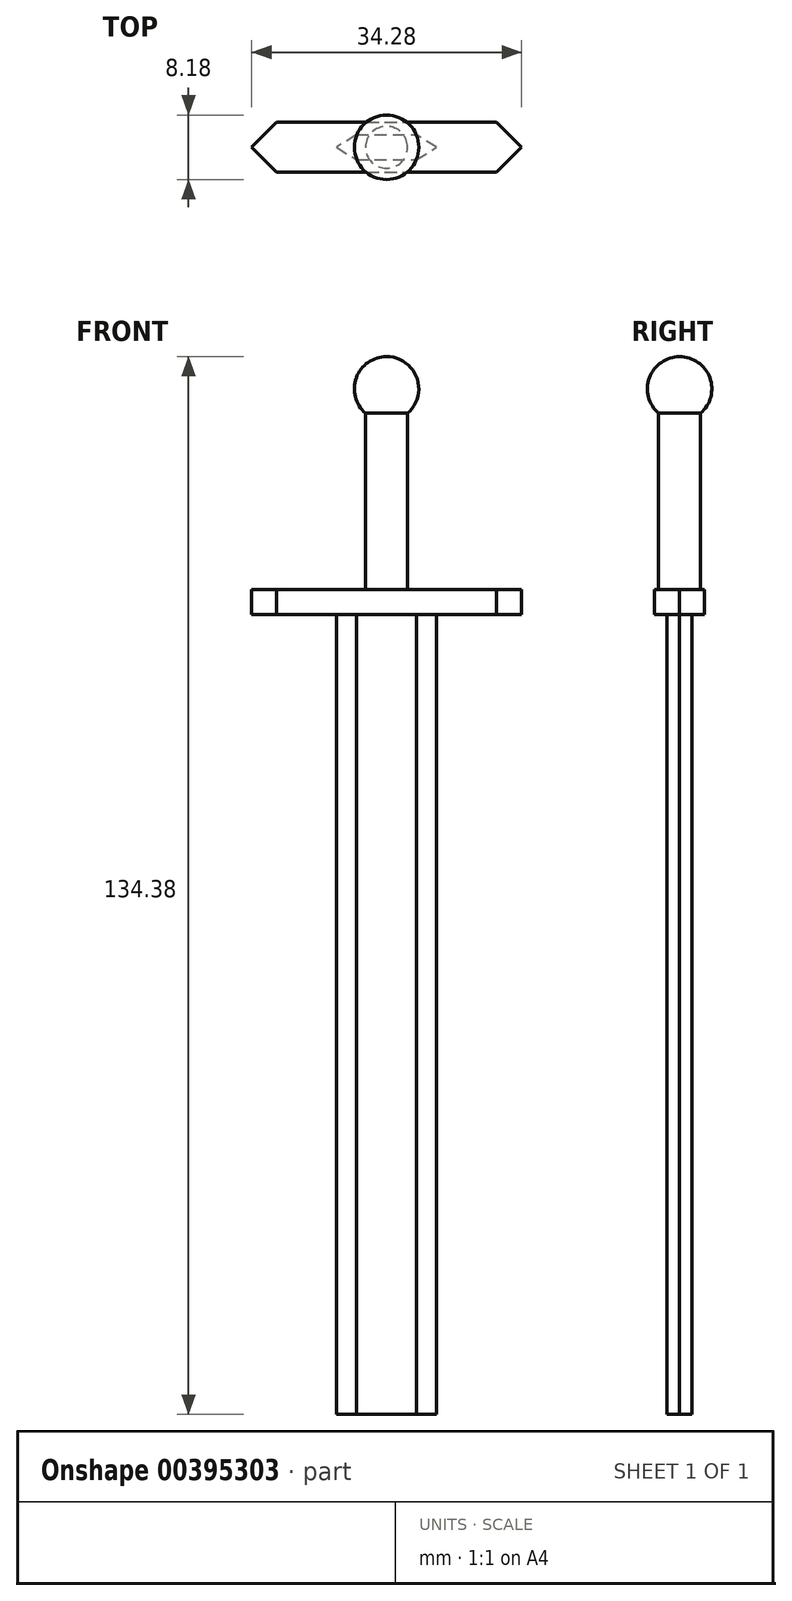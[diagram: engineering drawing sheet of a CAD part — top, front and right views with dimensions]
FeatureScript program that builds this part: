
annotation { "Feature Type Name" : "Feature", "Feature Type Description" : "" }
export const myFeature = defineFeature(function(context is Context, id is Id, definition is map)
    precondition{}
    {
        {
            var Q0;
            Q0=qCreatedBy(makeId("Top.planeOp"),FACE);
            var sketch = newSketch(context, id + "F0", { "sketchPlane" : qUnion([Q0])});
            skLineSegment(sketch, "E0.bottom", {"start": v(-3.81, 1.59) * mm, "end": v(0, 1.59) * mm});
            skLineSegment(sketch, "E0.top", {"start": v(-3.81, -1.59) * mm, "end": v(0, -1.59) * mm});
            skLineSegment(sketch, "E1", {"start": v(-3.81, 1.59) * mm, "end": v(-6.35, 0) * mm});
            skLineSegment(sketch, "E2", {"start": v(-6.35, 0) * mm, "end": v(-3.81, -1.59) * mm});
            skPoint(sketch, "E3.start.orphan", {"position": v(0, 1.59) * mm});
            skLineSegment(sketch, "E4", {"start": v(0, 1.59) * mm, "end": v(3.81, 1.59) * mm});
            skLineSegment(sketch, "E5", {"start": v(0, -1.59) * mm, "end": v(3.81, -1.59) * mm});
            skLineSegment(sketch, "E6", {"start": v(3.81, -1.59) * mm, "end": v(6.35, 0) * mm});
            skLineSegment(sketch, "E7", {"start": v(6.35, 0) * mm, "end": v(3.8, 1.59) * mm});
            skSolve(sketch);
        }
        {
            var Q0;
            Q0=makeQuery(id+"F0.imprint","IMPRINT",FACE,{"disambiguationData":[TD([[makeQuery(id+"F0.imprint","IMPRINT",EDGE,{"derivedFrom":sQuery(id+"F0.wireOp",EDGE,"E0.bottom")}),-1.0]])]});
            extrude(context, id + "F1", {"entities" : qUnion([Q0]), "depth" : 76.2 * mm});
        }
        {
            var Q0;
            Q0=makeQuery(id+"F1.opExtrude","CAP_FACE",FACE,{"disambiguationData":[OSD([sQuery(id+"F0.wireOp",EDGE,"E0.bottom"),sQuery(id+"F0.wireOp",EDGE,"E0.top"),sQuery(id+"F0.wireOp",EDGE,"E1"),sQuery(id+"F0.wireOp",EDGE,"E2"),sQuery(id+"F0.wireOp",EDGE,"E4"),sQuery(id+"F0.wireOp",EDGE,"E5"),sQuery(id+"F0.wireOp",EDGE,"E6"),sQuery(id+"F0.wireOp",EDGE,"E7")])],"isStart":false});
            var sketch = newSketch(context, id + "F2", { "sketchPlane" : qUnion([Q0])});
            skLineSegment(sketch, "E8.bottom", {"start": v(-19.05, 3.18) * mm, "end": v(19.05, 3.18) * mm});
            skLineSegment(sketch, "E8.top", {"start": v(-19.05, -3.18) * mm, "end": v(19.05, -3.18) * mm});
            skLineSegment(sketch, "E8.left", {"start": v(-19.05, 3.18) * mm, "end": v(-19.05, -3.18) * mm});
            skLineSegment(sketch, "E8.right", {"start": v(19.05, 3.18) * mm, "end": v(19.05, -3.18) * mm});
            skSolve(sketch);
        }
        {
            var Q0;
            Q0 = qSketchRegion(id + "F2", true);
            extrude(context, id + "F3", {"entities" : qUnion([Q0]), "operationType" : NewBodyOperationType.ADD, "depth" : 3.17 * mm});
        }
        {
            var Q0;
            Q0=makeQuery(id+"F3.opExtrude","SWEPT_EDGE",EDGE,{"disambiguationData":[OSD([sQuery(id+"F2.wireOp",EDGE,"E8.top"),sQuery(id+"F2.wireOp",EDGE,"E8.right")])]});
            var Q1;
            Q1=makeQuery(id+"F3.opExtrude","SWEPT_EDGE",EDGE,{"disambiguationData":[OSD([sQuery(id+"F2.wireOp",EDGE,"E8.bottom"),sQuery(id+"F2.wireOp",EDGE,"E8.right")])]});
            var Q2;
            Q2=makeQuery(id+"F3.opExtrude","SWEPT_EDGE",EDGE,{"disambiguationData":[OSD([sQuery(id+"F2.wireOp",EDGE,"E8.top"),sQuery(id+"F2.wireOp",EDGE,"E8.left")])]});
            var Q3;
            Q3=makeQuery(id+"F3.opExtrude","SWEPT_EDGE",EDGE,{"disambiguationData":[OSD([sQuery(id+"F2.wireOp",EDGE,"E8.bottom"),sQuery(id+"F2.wireOp",EDGE,"E8.left")])]});
            chamfer(context, id + "F4", {"entities" : qUnion([Q0, Q1, Q2, Q3]), "width" : 5.08 * mm, "tangentPropagation" : true});
        }
        {
            var Q0;
            Q0=makeQuery(id+"F3.opExtrude","CAP_FACE",FACE,{"disambiguationData":[OSD([sQuery(id+"F2.wireOp",EDGE,"E8.bottom"),sQuery(id+"F2.wireOp",EDGE,"E8.top"),sQuery(id+"F2.wireOp",EDGE,"E8.left"),sQuery(id+"F2.wireOp",EDGE,"E8.right")])],"isStart":false});
            var sketch = newSketch(context, id + "F5", { "sketchPlane" : qUnion([Q0])});
            skCircle(sketch, "E9", {"center": v(0, 0) * mm, "radius": 2.66 * mm});
            skSolve(sketch);
        }
        {
            var Q0;
            Q0 = qSketchRegion(id + "F5", true);
            extrude(context, id + "F6", {"entities" : qUnion([Q0]), "operationType" : NewBodyOperationType.ADD, "depth" : 25.4 * mm});
        }
        {
            var Q0;
            Q0=qCreatedBy(makeId("Front.planeOp"),FACE);
            var sketch = newSketch(context, id + "F7", { "sketchPlane" : qUnion([Q0])});
            skArc(sketch, "E10", {"start": v(0, 100.8) * mm, "mid": v(4.1, 104.89) * mm, "end": v(0, 108.98) * mm});
            skLineSegment(sketch, "E11", {"start": v(0, 108.98) * mm, "end": v(0, 100.8) * mm});
            skSolve(sketch);
        }
        {
            var Q0;
            Q0=makeQuery(id+"F7.imprint","IMPRINT",FACE,{"disambiguationData":[TD([[makeQuery(id+"F7.imprint","IMPRINT",EDGE,{"derivedFrom":sQuery(id+"F7.wireOp",EDGE,"E10")}),1.0]])]});
            var sketch = newSketch(context, id + "F8", { "sketchPlane" : qUnion([Q0])});
            skLineSegment(sketch, "E12", {"start": v(0, 97.72) * mm, "end": v(0, 113.92) * mm, "construction": true});
            skSolve(sketch);
        }
        {
            var Q0;
            Q0 = qSketchRegion(id + "F7", true);
            var Q1;
            Q1=sQuery(id+"F8.wireOp",EDGE,"E12");
            revolve(context, id + "F9", {"operationType" : NewBodyOperationType.ADD, "entities" : qUnion([Q0]), "axis" : qUnion([Q1]), "revolveType" : RevolveType.FULL});
        }
        {
            var Q0;
            Q0=makeQuery(id+"F1.opExtrude","CAP_FACE",FACE,{"disambiguationData":[OSD([sQuery(id+"F0.wireOp",EDGE,"E0.bottom"),sQuery(id+"F0.wireOp",EDGE,"E0.top"),sQuery(id+"F0.wireOp",EDGE,"E1"),sQuery(id+"F0.wireOp",EDGE,"E2"),sQuery(id+"F0.wireOp",EDGE,"E4"),sQuery(id+"F0.wireOp",EDGE,"E5"),sQuery(id+"F0.wireOp",EDGE,"E6"),sQuery(id+"F0.wireOp",EDGE,"E7")])],"isStart":true});
            extrude(context, id + "F10", {"entities" : qUnion([Q0]), "operationType" : NewBodyOperationType.ADD, "depth" : 25.4 * mm});
        }
    });
